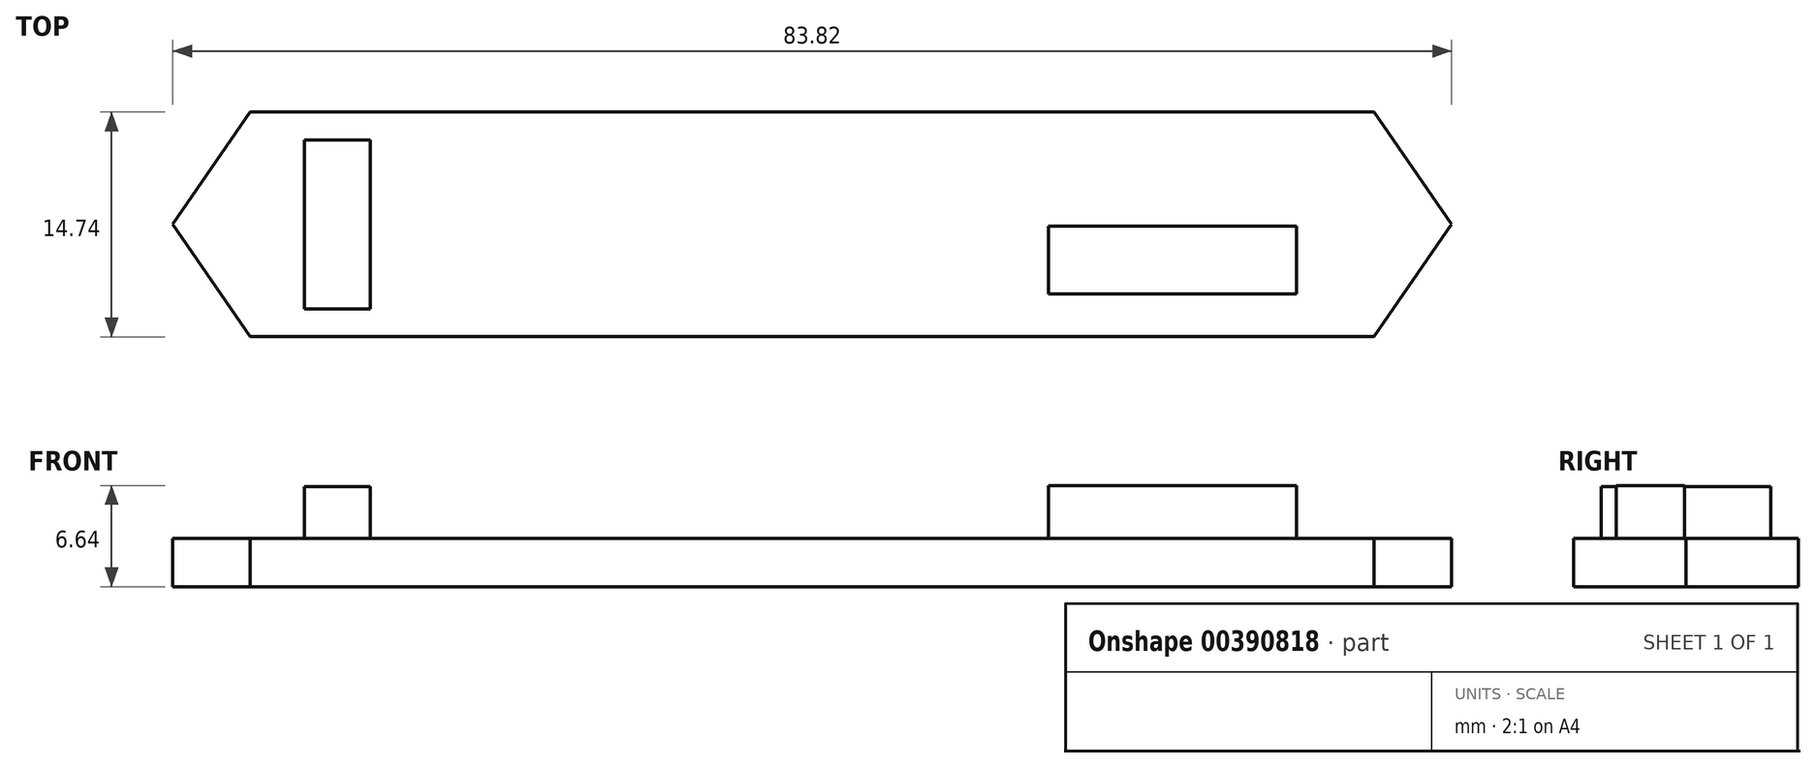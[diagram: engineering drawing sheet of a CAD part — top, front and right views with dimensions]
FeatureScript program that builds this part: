
annotation { "Feature Type Name" : "Feature", "Feature Type Description" : "" }
export const myFeature = defineFeature(function(context is Context, id is Id, definition is map)
    precondition{}
    {
        {
            var Q0;
            Q0=qCreatedBy(makeId("Top.planeOp"),FACE);
            var sketch = newSketch(context, id + "F0", { "sketchPlane" : qUnion([Q0])});
            skLineSegment(sketch, "E0.bottom", {"start": v(-36.83, 7.37) * mm, "end": v(36.83, 7.37) * mm});
            skLineSegment(sketch, "E0.top", {"start": v(-36.83, -7.37) * mm, "end": v(36.83, -7.37) * mm});
            skPoint(sketch, "E0.middle", {"position": v(0, 0) * mm});
            skLineSegment(sketch, "E1", {"start": v(41.9, 0) * mm, "end": v(36.83, -7.37) * mm});
            skLineSegment(sketch, "E2.MirrorCS", {"start": v(41.9, 0) * mm, "end": v(36.83, 7.37) * mm});
            skLineSegment(sketch, "E3.MirrorCS", {"start": v(-41.9, 0) * mm, "end": v(-36.83, 7.37) * mm});
            skLineSegment(sketch, "E4.MirrorCS", {"start": v(-41.91, 0) * mm, "end": v(-36.83, -7.37) * mm});
            skLineSegment(sketch, "E5.bottom", {"start": v(15.5, -0.1) * mm, "end": v(31.75, -0.1) * mm});
            skLineSegment(sketch, "E5.top", {"start": v(15.5, -4.57) * mm, "end": v(31.75, -4.57) * mm});
            skLineSegment(sketch, "E5.left", {"start": v(15.5, -0.1) * mm, "end": v(15.5, -4.57) * mm});
            skLineSegment(sketch, "E5.right", {"start": v(31.75, -0.1) * mm, "end": v(31.75, -4.57) * mm});
            skLineSegment(sketch, "E6.bottom", {"start": v(-33.27, 5.55) * mm, "end": v(-28.96, 5.55) * mm});
            skLineSegment(sketch, "E6.top", {"start": v(-33.27, -5.55) * mm, "end": v(-28.96, -5.55) * mm});
            skLineSegment(sketch, "E6.left", {"start": v(-33.27, 5.55) * mm, "end": v(-33.27, -5.55) * mm});
            skLineSegment(sketch, "E6.right", {"start": v(-28.96, 5.55) * mm, "end": v(-28.96, -5.55) * mm});
            skLineSegment(sketch, "E7", {"start": v(-69.06, 0) * mm, "end": v(67.9, 0) * mm, "construction": true});
            skSolve(sketch);
        }
        {
            var Q0;
            Q0 = qSketchRegion(id + "F0", true);
            var Q1;
            Q1=makeQuery(id+"F0.imprint","IMPRINT",FACE,{"disambiguationData":[TD([[makeQuery(id+"F0.imprint","IMPRINT",EDGE,{"derivedFrom":sQuery(id+"F0.wireOp",EDGE,"E6.bottom")}),-1.0]])]});
            var Q2;
            Q2=makeQuery(id+"F0.imprint","IMPRINT",FACE,{"disambiguationData":[TD([[makeQuery(id+"F0.imprint","IMPRINT",EDGE,{"derivedFrom":sQuery(id+"F0.wireOp",EDGE,"E5.bottom")}),-1.0]])]});
            extrude(context, id + "F1", {"entities" : qUnion([Q0, Q1, Q2]), "oppositeDirection" : true, "depth" : 3.16 * mm});
        }
        {
            var Q0;
            Q0=makeQuery(id+"F0.imprint","IMPRINT",FACE,{"disambiguationData":[TD([[makeQuery(id+"F0.imprint","IMPRINT",EDGE,{"derivedFrom":sQuery(id+"F0.wireOp",EDGE,"E5.bottom")}),-1.0]])]});
            extrude(context, id + "F2", {"entities" : qUnion([Q0]), "operationType" : NewBodyOperationType.ADD, "depth" : 3.48 * mm});
        }
        {
            var Q0;
            Q0=makeQuery(id+"F0.imprint","IMPRINT",FACE,{"disambiguationData":[TD([[makeQuery(id+"F0.imprint","IMPRINT",EDGE,{"derivedFrom":sQuery(id+"F0.wireOp",EDGE,"E6.bottom")}),-1.0]])]});
            extrude(context, id + "F3", {"entities" : qUnion([Q0]), "operationType" : NewBodyOperationType.ADD, "depth" : 3.4 * mm});
        }
    });
